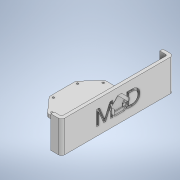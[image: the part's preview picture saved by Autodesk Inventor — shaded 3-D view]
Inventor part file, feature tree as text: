
AUTODESK INVENTOR PART (.ipt)
format: ipt  version: 2020.4 (Build 244396000, 396)  size: 371,200 bytes
history: native  units: in
note: dims shown in document units (in); Inventor stores cm internally (conversion verified against a paired STEP export)
features: extrude x9, sketch x7, fillet x2, hole x1, chamfer x1
ambient origin geometry x8: Origin, YZ Plane, XZ Plane, XY Plane, X Axis, Y Axis, Z Axis, Center Point
bodies: Solid1 (feature_tree)
feature tree (20):
  extrude  "Extrusion1"  Depth=1.2598in
  hole  "Hole1"  [1 undecoded]
  extrude  "Extrusion2"  Depth=0.1575in
  chamfer  "Chamfer1"  Distance=2.874in
  fillet  "Fillet1"  Radius=0.7874in
  fillet  "Fillet2"  Radius=0.1575in
  extrude  "Extrusion3"  Depth=1.3386in
  extrude  "Extrusion4"  Depth=0.0236in
  sketch  "Sketch6"  dims[d17=2.6772in]
  extrude  "Extrusion6"  Depth=0.0236in
  extrude  "Extrusion10"  Depth=0.1575in
  extrude  "Extrusion13"  Depth=0.0236in
  extrude  "Extrusion14"  Depth=0.1575in
  extrude  "Extrusion15"  Depth=0.0236in
  sketch  "Sketch1"  dims[d1=1.3386in d2=1.2598in]
  sketch  "Sketch2"  dims[d3=0.6299in d4=0.6299in]
  sketch  "Sketch3"  dims[d6=0.315in d12=0.1575in]
  sketch  "Sketch4"  dims[d13=0.1575in]
  sketch  "Sketch5"  dims[d15=0.1575in]
  sketch  "Sketch8"  dims[d18=2.9921in d19=2.874in d21=0.7874in d22=0.1575in d23=0.0in d24=0.0984in d25=0.2362in d26=0.1575in d27=0.0787in d28=90.0deg d29=0.315in d30=0.8108in d31=1.3386in d33=0.7874in d34=0.6299in d35=0.1575in d36=0.6299in d37=0.1575in d38=0.7874in d39=1.3386in d40=2.9921in d41=2.0866in d42=5.5118in d43=0.1654in d45=1.4961in d46=0.0in d47=0.1575in d48=0.0in d49=0.0787in d50=0.0787in d51=45.0deg d52=2.7559in d53=0.3937in d54=0.3937in d55=0.0787in d56=0.0787in d117=0.0709in d118=0.0709in d119=0.0984in d120=0.0984in d124=0.7756in d136=0.0653in d137=0.0653in d143=0.5961in d144=0.5961in d147=0.1307in d161=0.1063in d180=0.1063in d185=0.1601in d186=0.1601in d187=0.439in d236=3.1798in d237=0.1102in d238=0.0in d259=0.1063in d262=0.1063in d263=0.1063in d267=0.7368in d269=0.1921in d274=0.2815in d276=0.1921in d279=0.1102in d280=0.0in d311=0.1457in d316=0.1457in d366=0.4921in d389=0.1417in d390=0.1417in d406=0.0803in d434=0.1228in d442=0.4247in d445=0.1102in d446=0.0in d447=0.1417in d448=0.8661in d455=0.1102in d456=0.0in d461=0.0709in d462=0.0in d463=0.0472in d464=0.0in d465=0.0236in d466=0.0in d44=0.0148in d443=0.0197in d444=0.0344in d449=0.0197in d450=0.0344in d451=0.0197in d452=0.0344in d453=0.0197in d454=0.0344in d457=0.0197in d458=0.0344in d459=0.0197in d460=0.0344in]
note: 1 required parameter value undecoded (feature->parameter linkage not recoverable at this tier; creation-order binding heuristic only, values carry confidence <= 0.55)
